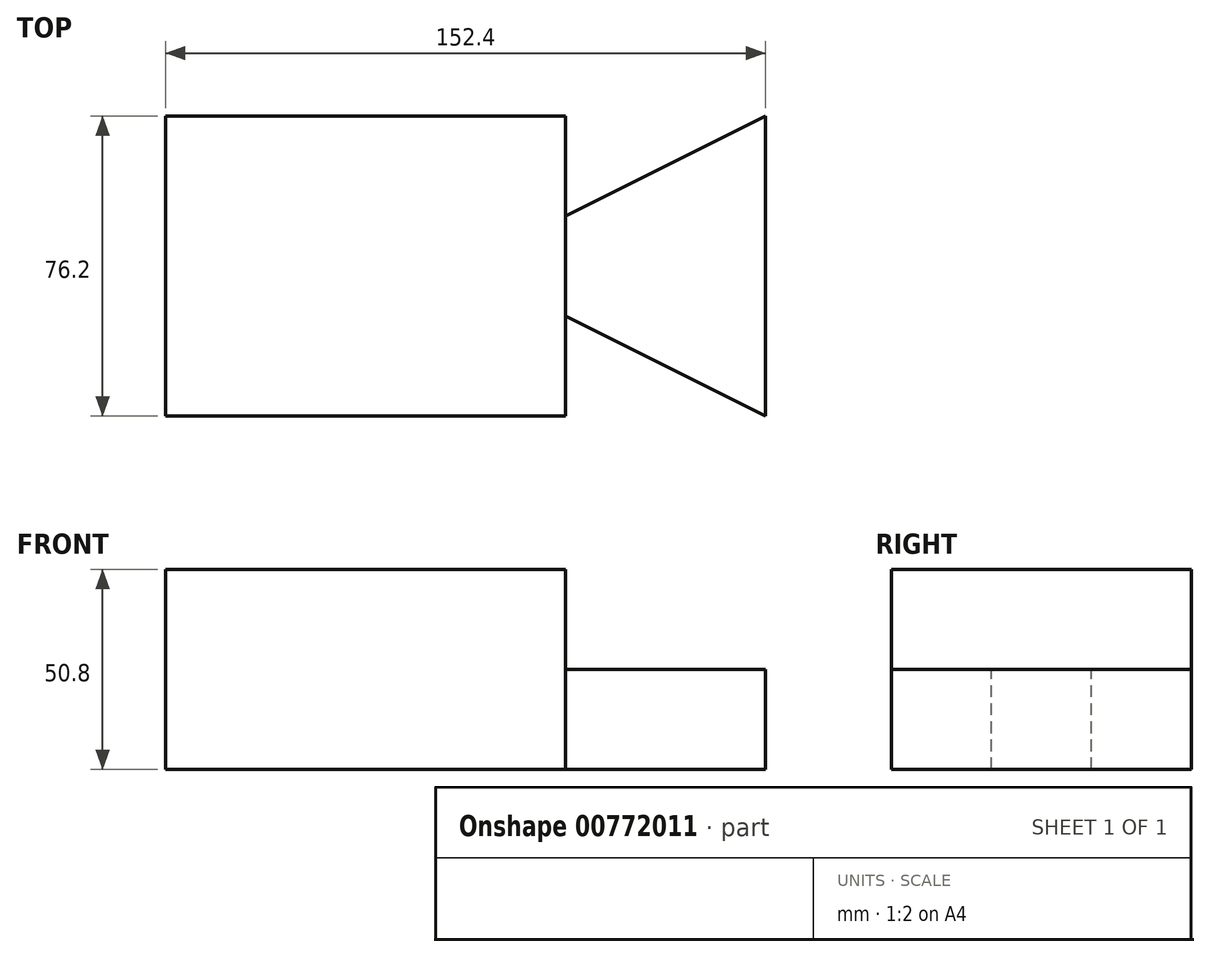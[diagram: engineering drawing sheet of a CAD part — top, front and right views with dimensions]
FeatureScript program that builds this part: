
annotation { "Feature Type Name" : "Feature", "Feature Type Description" : "" }
export const myFeature = defineFeature(function(context is Context, id is Id, definition is map)
    precondition{}
    {
        {
            var Q0;
            Q0=qCreatedBy(makeId("Front.planeOp"),FACE);
            var sketch = newSketch(context, id + "F0", { "sketchPlane" : qUnion([Q0])});
            skLineSegment(sketch, "E0", {"start": v(0, 0) * mm, "end": v(152.4, 0) * mm});
            skLineSegment(sketch, "E1", {"start": v(152.4, 0) * mm, "end": v(152.4, 50.8) * mm});
            skLineSegment(sketch, "E2", {"start": v(152.4, 50.8) * mm, "end": v(0, 50.8) * mm});
            skLineSegment(sketch, "E3", {"start": v(0, 50.8) * mm, "end": v(0, 0) * mm});
            skSolve(sketch);
        }
        {
            var Q0;
            Q0=makeQuery(id+"F0.imprint","IMPRINT",FACE,{"disambiguationData":[TD([[makeQuery(id+"F0.imprint","IMPRINT",EDGE,{"derivedFrom":sQuery(id+"F0.wireOp",EDGE,"E0")}),1.0]])]});
            extrude(context, id + "F1", {"entities" : qUnion([Q0]), "depth" : 76.2 * mm, "offsetDistance" : 25.4 * mm});
        }
        {
            var Q0;
            Q0=makeQuery(id+"F1.opExtrude","SWEPT_FACE",FACE,{"disambiguationData":[OSD([sQuery(id+"F0.wireOp",EDGE,"E1")])]});
            var sketch = newSketch(context, id + "F2", { "sketchPlane" : qUnion([Q0])});
            skLineSegment(sketch, "E4", {"start": v(-76.2, 50.8) * mm, "end": v(0, 50.8) * mm});
            skLineSegment(sketch, "E5", {"start": v(0, 50.8) * mm, "end": v(0, 25.4) * mm});
            skLineSegment(sketch, "E6", {"start": v(0, 25.4) * mm, "end": v(-76.2, 25.4) * mm});
            skLineSegment(sketch, "E7", {"start": v(-76.2, 25.4) * mm, "end": v(-76.2, 50.8) * mm});
            skSolve(sketch);
        }
        {
            var Q0;
            Q0=makeQuery(id+"F2.imprint","IMPRINT",FACE,{"disambiguationData":[TD([[makeQuery(id+"F2.imprint","IMPRINT",EDGE,{"derivedFrom":sQuery(id+"F2.wireOp",EDGE,"E4")}),-1.0]])]});
            extrude(context, id + "F3", {"entities" : qUnion([Q0]), "operationType" : NewBodyOperationType.REMOVE, "oppositeDirection" : true, "depth" : 50.8 * mm, "offsetDistance" : 25.4 * mm});
        }
        {
            var Q0;
            Q0=makeQuery(id+"F3.boolean.opBoolean","COPY",FACE,{"derivedFrom":makeQuery(id+"F3.opExtrude","SWEPT_FACE",FACE,{"disambiguationData":[OSD([sQuery(id+"F2.wireOp",EDGE,"E6")])]})});
            var sketch = newSketch(context, id + "F4", { "sketchPlane" : qUnion([Q0])});
            skLineSegment(sketch, "E8", {"start": v(101.6, -76.2) * mm, "end": v(101.6, -50.8) * mm});
            skLineSegment(sketch, "E9", {"start": v(101.6, -50.8) * mm, "end": v(152.4, -76.2) * mm});
            skLineSegment(sketch, "E10", {"start": v(152.4, -76.2) * mm, "end": v(101.6, -76.2) * mm});
            skLineSegment(sketch, "E11", {"start": v(101.6, 0) * mm, "end": v(101.6, -25.4) * mm});
            skLineSegment(sketch, "E12", {"start": v(101.6, -25.4) * mm, "end": v(152.4, 0) * mm});
            skLineSegment(sketch, "E13", {"start": v(152.4, 0) * mm, "end": v(101.6, 0) * mm});
            skSolve(sketch);
        }
        {
            var Q0;
            Q0=makeQuery(id+"F4.imprint","IMPRINT",FACE,{"disambiguationData":[TD([[makeQuery(id+"F4.imprint","IMPRINT",EDGE,{"derivedFrom":sQuery(id+"F4.wireOp",EDGE,"E8")}),1.0]])]});
            extrude(context, id + "F5", {"entities" : qUnion([Q0]), "operationType" : NewBodyOperationType.REMOVE, "oppositeDirection" : true, "depth" : 25.4 * mm, "offsetDistance" : 25.4 * mm});
        }
        {
            var Q0;
            Q0=makeQuery(id+"F3.boolean.opBoolean","COPY",FACE,{"derivedFrom":makeQuery(id+"F3.opExtrude","SWEPT_FACE",FACE,{"disambiguationData":[OSD([sQuery(id+"F2.wireOp",EDGE,"E6")])]})});
            var sketch = newSketch(context, id + "F6", { "sketchPlane" : qUnion([Q0])});
            skLineSegment(sketch, "E14", {"start": v(101.6, 0) * mm, "end": v(101.6, -25.4) * mm});
            skLineSegment(sketch, "E15", {"start": v(101.6, -25.4) * mm, "end": v(152.4, 0) * mm});
            skLineSegment(sketch, "E16", {"start": v(152.4, 0) * mm, "end": v(101.6, 0) * mm});
            skSolve(sketch);
        }
        {
            var Q0;
            Q0=makeQuery(id+"F6.imprint","IMPRINT",FACE,{"disambiguationData":[TD([[makeQuery(id+"F6.imprint","IMPRINT",EDGE,{"derivedFrom":sQuery(id+"F6.wireOp",EDGE,"E14")}),1.0]])]});
            extrude(context, id + "F7", {"entities" : qUnion([Q0]), "operationType" : NewBodyOperationType.REMOVE, "oppositeDirection" : true, "depth" : 25.4 * mm, "offsetDistance" : 25.4 * mm});
        }
    });
